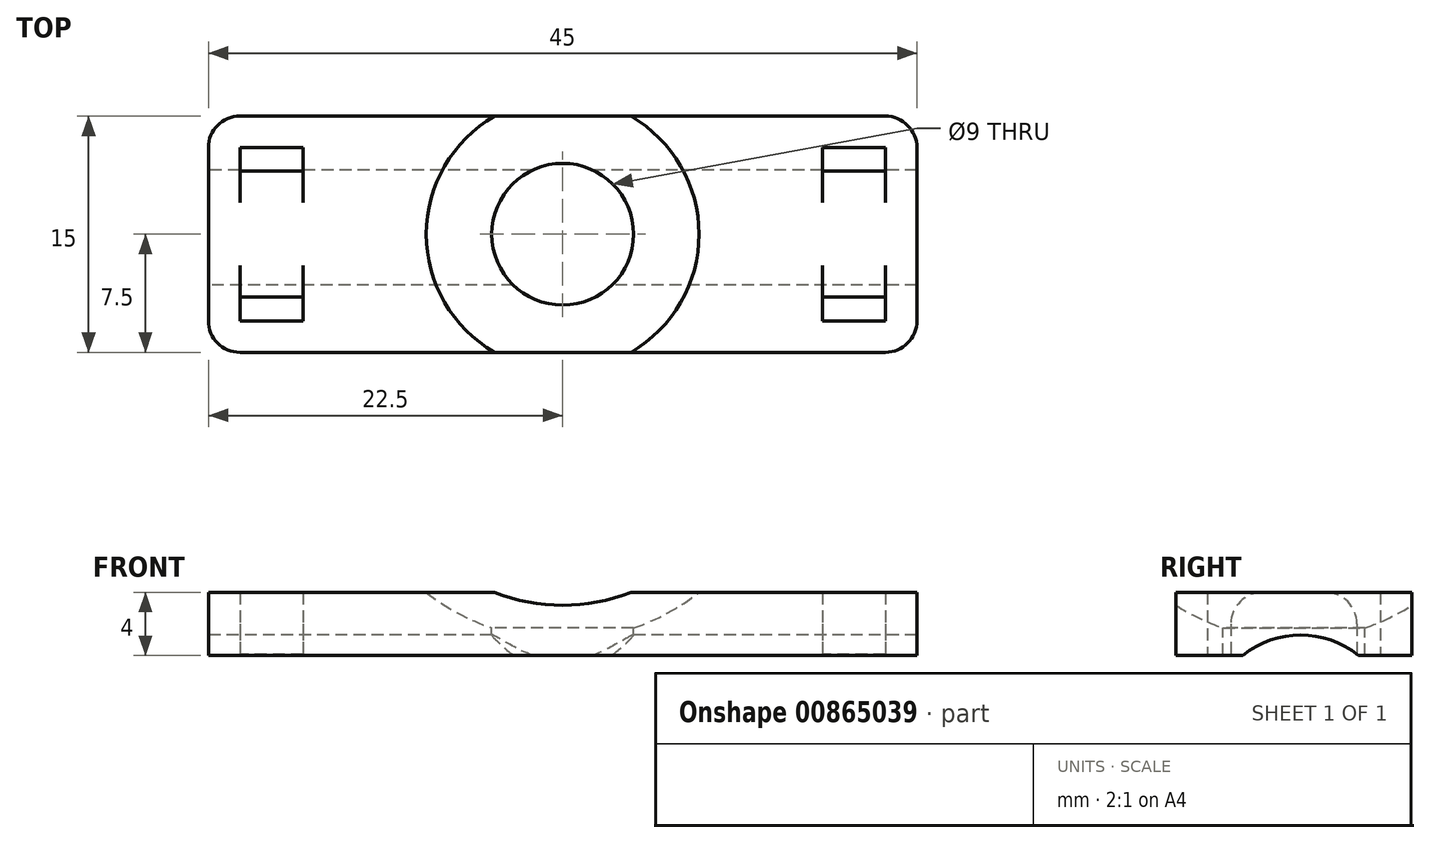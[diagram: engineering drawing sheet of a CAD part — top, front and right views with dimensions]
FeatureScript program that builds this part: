
annotation { "Feature Type Name" : "Feature", "Feature Type Description" : "" }
export const myFeature = defineFeature(function(context is Context, id is Id, definition is map)
    precondition{}
    {
        {
            assignVariable(context, id + "F0", {"name" : "x", "anyValue" : 15});
        }
        {
            var Q0;
            Q0=qCreatedBy(makeId("Top.planeOp"),FACE);
            var sketch = newSketch(context, id + "F1", { "sketchPlane" : qUnion([Q0])});
            skLineSegment(sketch, "E0.bottom", {"start": v(22.5, -7.5) * mm, "end": v(-22.5, -7.5) * mm});
            skLineSegment(sketch, "E0.top", {"start": v(22.5, 7.5) * mm, "end": v(-22.5, 7.5) * mm});
            skLineSegment(sketch, "E0.left", {"start": v(22.5, -7.5) * mm, "end": v(22.5, 7.5) * mm});
            skLineSegment(sketch, "E0.right", {"start": v(-22.5, -7.5) * mm, "end": v(-22.5, 7.5) * mm});
            skPoint(sketch, "E0.middle", {"position": v(0, 0) * mm});
            skSolve(sketch);
        }
        {
            var Q0;
            Q0=makeQuery(id+"F1.imprint","IMPRINT",FACE,{"disambiguationData":[TD([[makeQuery(id+"F1.imprint","IMPRINT",EDGE,{"derivedFrom":sQuery(id+"F1.wireOp",EDGE,"E0.bottom")}),-1.0]])]});
            extrude(context, id + "F2", {"entities" : qUnion([Q0]), "oppositeDirection" : true, "depth" : 4 * mm, "offsetDistance" : 25 * mm});
        }
        {
            var Q0;
            Q0=makeQuery(id+"F2.opExtrude","CAP_FACE",FACE,{"disambiguationData":[OSD([sQuery(id+"F1.wireOp",EDGE,"E0.bottom"),sQuery(id+"F1.wireOp",EDGE,"E0.top"),sQuery(id+"F1.wireOp",EDGE,"E0.left"),sQuery(id+"F1.wireOp",EDGE,"E0.right")])],"isStart":false});
            cPlane(context, id + "F3", {"entities" : qUnion([Q0]), "cplaneType" : CPlaneType.OFFSET, "offset" : (getVariable(context, 'x')) * mm, "oppositeDirection" : true, "width" : 150 * mm, "height" : 150 * mm});
        }
        {
            var Q0;
            Q0=qCreatedBy(id+"F3.planeOp",FACE);
            var sketch = newSketch(context, id + "F4", { "sketchPlane" : qUnion([Q0])});
            skCircle(sketch, "E1", {"center": v(0, 0) * mm, "radius": 14 * mm});
            skLineSegment(sketch, "E2", {"start": v(-14, 0) * mm, "end": v(14, 0) * mm});
            skSolve(sketch);
        }
        {
            var Q0;
            {var subQ0=sQuery(id+"F4.wireOp",EDGE,"E2");Q0=makeQuery(id+"F4.imprint","IMPRINT",FACE,{"disambiguationData":[TD([[makeQuery(id+"F4.imprint","IMPRINT",EDGE,{"derivedFrom":subQ0}),1.0]])]});}
            var Q1;
            Q1=sQuery(id+"F4.wireOp",EDGE,"E2");
            revolve(context, id + "F5", {"operationType" : NewBodyOperationType.REMOVE, "surfaceOperationType" : NewSurfaceOperationType.NEW, "entities" : qUnion([Q0]), "axis" : qUnion([Q1]), "revolveType" : RevolveType.FULL, "oppositeDirection" : true});
        }
        {
            var Q0;
            Q0=qCreatedBy(id+"F3.planeOp",FACE);
            var sketch = newSketch(context, id + "F6", { "sketchPlane" : qUnion([Q0])});
            skCircle(sketch, "E3", {"center": v(0, 0) * mm, "radius": 4.5 * mm});
            skSolve(sketch);
        }
        {
            var Q0;
            Q0 = qSketchRegion(id + "F6", true);
            extrude(context, id + "F7", {"entities" : qUnion([Q0]), "operationType" : NewBodyOperationType.REMOVE, "depth" : 16 * mm, "offsetDistance" : 25 * mm});
        }
        {
            var Q0;
            Q0=makeQuery(id+"F2.opExtrude","CAP_FACE",FACE,{"disambiguationData":[OSD([sQuery(id+"F1.wireOp",EDGE,"E0.bottom"),sQuery(id+"F1.wireOp",EDGE,"E0.top"),sQuery(id+"F1.wireOp",EDGE,"E0.left"),sQuery(id+"F1.wireOp",EDGE,"E0.right")])],"isStart":false});
            var sketch = newSketch(context, id + "F8", { "sketchPlane" : qUnion([Q0])});
            skLineSegment(sketch, "E4.bottom", {"start": v(-16.5, 4) * mm, "end": v(-20.5, 4) * mm});
            skLineSegment(sketch, "E4.top", {"start": v(-16.5, 5.5) * mm, "end": v(-20.5, 5.5) * mm});
            skLineSegment(sketch, "E4.left", {"start": v(-16.5, 4) * mm, "end": v(-16.5, 5.5) * mm});
            skLineSegment(sketch, "E4.right", {"start": v(-20.5, 4) * mm, "end": v(-20.5, 5.5) * mm});
            skPoint(sketch, "E4.middle", {"position": v(-18.5, 4.75) * mm});
            skLineSegment(sketch, "E5.MirrorCS", {"start": v(16.5, 4) * mm, "end": v(16.5, 5.5) * mm});
            skLineSegment(sketch, "E6.MirrorCS", {"start": v(16.5, 5.5) * mm, "end": v(20.5, 5.5) * mm});
            skLineSegment(sketch, "E7.MirrorCS", {"start": v(20.5, 4) * mm, "end": v(20.5, 5.5) * mm});
            skLineSegment(sketch, "E8.MirrorCS", {"start": v(16.5, 4) * mm, "end": v(20.5, 4) * mm});
            skLineSegment(sketch, "E9.MirrorCS", {"start": v(-16.5, -4) * mm, "end": v(-16.5, -5.5) * mm});
            skLineSegment(sketch, "E10.MirrorCS", {"start": v(-16.5, -5.5) * mm, "end": v(-20.5, -5.5) * mm});
            skLineSegment(sketch, "E11.MirrorCS", {"start": v(-20.5, -4) * mm, "end": v(-20.5, -5.5) * mm});
            skLineSegment(sketch, "E12.MirrorCS", {"start": v(-16.5, -4) * mm, "end": v(-20.5, -4) * mm});
            skLineSegment(sketch, "E13.MirrorCS", {"start": v(16.5, -4) * mm, "end": v(16.5, -5.5) * mm});
            skLineSegment(sketch, "E14.MirrorCS", {"start": v(16.5, -5.5) * mm, "end": v(20.5, -5.5) * mm});
            skLineSegment(sketch, "E15.MirrorCS", {"start": v(20.5, -4) * mm, "end": v(20.5, -5.5) * mm});
            skLineSegment(sketch, "E16.MirrorCS", {"start": v(16.5, -4) * mm, "end": v(20.5, -4) * mm});
            skSolve(sketch);
        }
        {
            var Q0;
            Q0 = qSketchRegion(id + "F8", true);
            extrude(context, id + "F9", {"entities" : qUnion([Q0]), "operationType" : NewBodyOperationType.REMOVE, "oppositeDirection" : true, "depth" : 25 * mm, "offsetDistance" : 25 * mm});
        }
        {
            var Q0;
            {var subQ0=sQuery(id+"F1.wireOp",EDGE,"E0.bottom");var subQ1=sQuery(id+"F1.wireOp",EDGE,"E0.right");var subQ2=sQuery(id+"F1.wireOp",EDGE,"E0.top");Q0=makeQuery(id+"F9.boolean.opBoolean","INTERSECT",EDGE,{"derivedFrom":[makeQuery(id+"F5.boolean.opBoolean","SPLIT",FACE,{"disambiguationData":[TD([makeQuery(id+"F2.opExtrude","SWEPT_FACE",FACE,{"disambiguationData":[OSD([subQ1])]})])],"derivedFrom":makeQuery(id+"F2.opExtrude","CAP_FACE",FACE,{"disambiguationData":[OSD([subQ0,subQ2,sQuery(id+"F1.wireOp",EDGE,"E0.left"),subQ1])],"isStart":true})}),makeQuery(id+"F9.opExtrude","SWEPT_FACE",FACE,{"disambiguationData":[OSD([sQuery(id+"F8.wireOp",EDGE,"E4.bottom")])]})]});}
            var Q1;
            {var subQ0=sQuery(id+"F1.wireOp",EDGE,"E0.bottom");var subQ1=sQuery(id+"F1.wireOp",EDGE,"E0.top");var subQ2=sQuery(id+"F1.wireOp",EDGE,"E0.left");Q1=makeQuery(id+"F9.boolean.opBoolean","INTERSECT",EDGE,{"derivedFrom":[makeQuery(id+"F5.boolean.opBoolean","SPLIT",FACE,{"disambiguationData":[TD([makeQuery(id+"F2.opExtrude","SWEPT_FACE",FACE,{"disambiguationData":[OSD([subQ2])]})])],"derivedFrom":makeQuery(id+"F2.opExtrude","CAP_FACE",FACE,{"disambiguationData":[OSD([subQ0,subQ1,subQ2,sQuery(id+"F1.wireOp",EDGE,"E0.right")])],"isStart":true})}),makeQuery(id+"F9.opExtrude","SWEPT_FACE",FACE,{"disambiguationData":[OSD([sQuery(id+"F8.wireOp",EDGE,"E8.MirrorCS")])]})]});}
            var Q2;
            {var subQ0=sQuery(id+"F1.wireOp",EDGE,"E0.bottom");var subQ1=sQuery(id+"F1.wireOp",EDGE,"E0.top");var subQ2=sQuery(id+"F1.wireOp",EDGE,"E0.left");Q2=makeQuery(id+"F9.boolean.opBoolean","INTERSECT",EDGE,{"derivedFrom":[makeQuery(id+"F5.boolean.opBoolean","SPLIT",FACE,{"disambiguationData":[TD([makeQuery(id+"F2.opExtrude","SWEPT_FACE",FACE,{"disambiguationData":[OSD([subQ2])]})])],"derivedFrom":makeQuery(id+"F2.opExtrude","CAP_FACE",FACE,{"disambiguationData":[OSD([subQ0,subQ1,subQ2,sQuery(id+"F1.wireOp",EDGE,"E0.right")])],"isStart":true})}),makeQuery(id+"F9.opExtrude","SWEPT_FACE",FACE,{"disambiguationData":[OSD([sQuery(id+"F8.wireOp",EDGE,"E16.MirrorCS")])]})]});}
            var Q3;
            {var subQ0=sQuery(id+"F1.wireOp",EDGE,"E0.bottom");var subQ1=sQuery(id+"F1.wireOp",EDGE,"E0.right");var subQ2=sQuery(id+"F1.wireOp",EDGE,"E0.top");Q3=makeQuery(id+"F9.boolean.opBoolean","INTERSECT",EDGE,{"derivedFrom":[makeQuery(id+"F5.boolean.opBoolean","SPLIT",FACE,{"disambiguationData":[TD([makeQuery(id+"F2.opExtrude","SWEPT_FACE",FACE,{"disambiguationData":[OSD([subQ1])]})])],"derivedFrom":makeQuery(id+"F2.opExtrude","CAP_FACE",FACE,{"disambiguationData":[OSD([subQ0,subQ2,sQuery(id+"F1.wireOp",EDGE,"E0.left"),subQ1])],"isStart":true})}),makeQuery(id+"F9.opExtrude","SWEPT_FACE",FACE,{"disambiguationData":[OSD([sQuery(id+"F8.wireOp",EDGE,"E12.MirrorCS")])]})]});}
            fillet(context, id + "F10", {"entities" : qUnion([Q0, Q1, Q2, Q3]), "radius" : 2 * mm, "tangentPropagation" : true, "allowEdgeOverflow" : false});
        }
        {
            var Q0;
            Q0=makeQuery(id+"F2.opExtrude","SWEPT_EDGE",EDGE,{"disambiguationData":[OSD([sQuery(id+"F1.wireOp",EDGE,"E0.bottom"),sQuery(id+"F1.wireOp",EDGE,"E0.right")])]});
            var Q1;
            Q1=makeQuery(id+"F2.opExtrude","SWEPT_EDGE",EDGE,{"disambiguationData":[OSD([sQuery(id+"F1.wireOp",EDGE,"E0.bottom"),sQuery(id+"F1.wireOp",EDGE,"E0.left")])]});
            var Q2;
            Q2=makeQuery(id+"F2.opExtrude","SWEPT_EDGE",EDGE,{"disambiguationData":[OSD([sQuery(id+"F1.wireOp",EDGE,"E0.top"),sQuery(id+"F1.wireOp",EDGE,"E0.left")])]});
            var Q3;
            Q3=makeQuery(id+"F2.opExtrude","SWEPT_EDGE",EDGE,{"disambiguationData":[OSD([sQuery(id+"F1.wireOp",EDGE,"E0.top"),sQuery(id+"F1.wireOp",EDGE,"E0.right")])]});
            fillet(context, id + "F11", {"entities" : qUnion([Q0, Q1, Q2, Q3]), "radius" : 2 * mm, "tangentPropagation" : true, "allowEdgeOverflow" : false});
        }
        {
            var Q0;
            Q0=makeQuery(id+"F2.opExtrude","SWEPT_FACE",FACE,{"disambiguationData":[OSD([sQuery(id+"F1.wireOp",EDGE,"E0.right")])]});
            var sketch = newSketch(context, id + "F12", { "sketchPlane" : qUnion([Q0])});
            skLineSegment(sketch, "E17", {"start": v(-6.3, -4) * mm, "end": v(6.3, -4) * mm});
            skCircle(sketch, "E18", {"center": v(-0.42, -8.5) * mm, "radius": 5.8 * mm});
            skSolve(sketch);
        }
        {
            var Q0;
            {var subQ0=sQuery(id+"F12.wireOp",EDGE,"E18");var subQ1=sQuery(id+"F12.wireOp",EDGE,"E17");var subQ2=makeQuery(id+"F12.imprint","INTERSECT",VERTEX,{"disambiguationData":[OD(0.0)],"derivedFrom":[subQ1,subQ0]});Q0=makeQuery(id+"F12.imprint","IMPRINT",FACE,{"disambiguationData":[TD([[makeQuery(id+"F12.imprint","IMPRINT",EDGE,{"disambiguationData":[TD([[subQ2,-1.0]])],"derivedFrom":subQ1}),-1.0]])]});}
            extrude(context, id + "F13", {"entities" : qUnion([Q0]), "operationType" : NewBodyOperationType.REMOVE, "oppositeDirection" : true, "depth" : 50 * mm, "offsetDistance" : 25 * mm});
        }
    });
